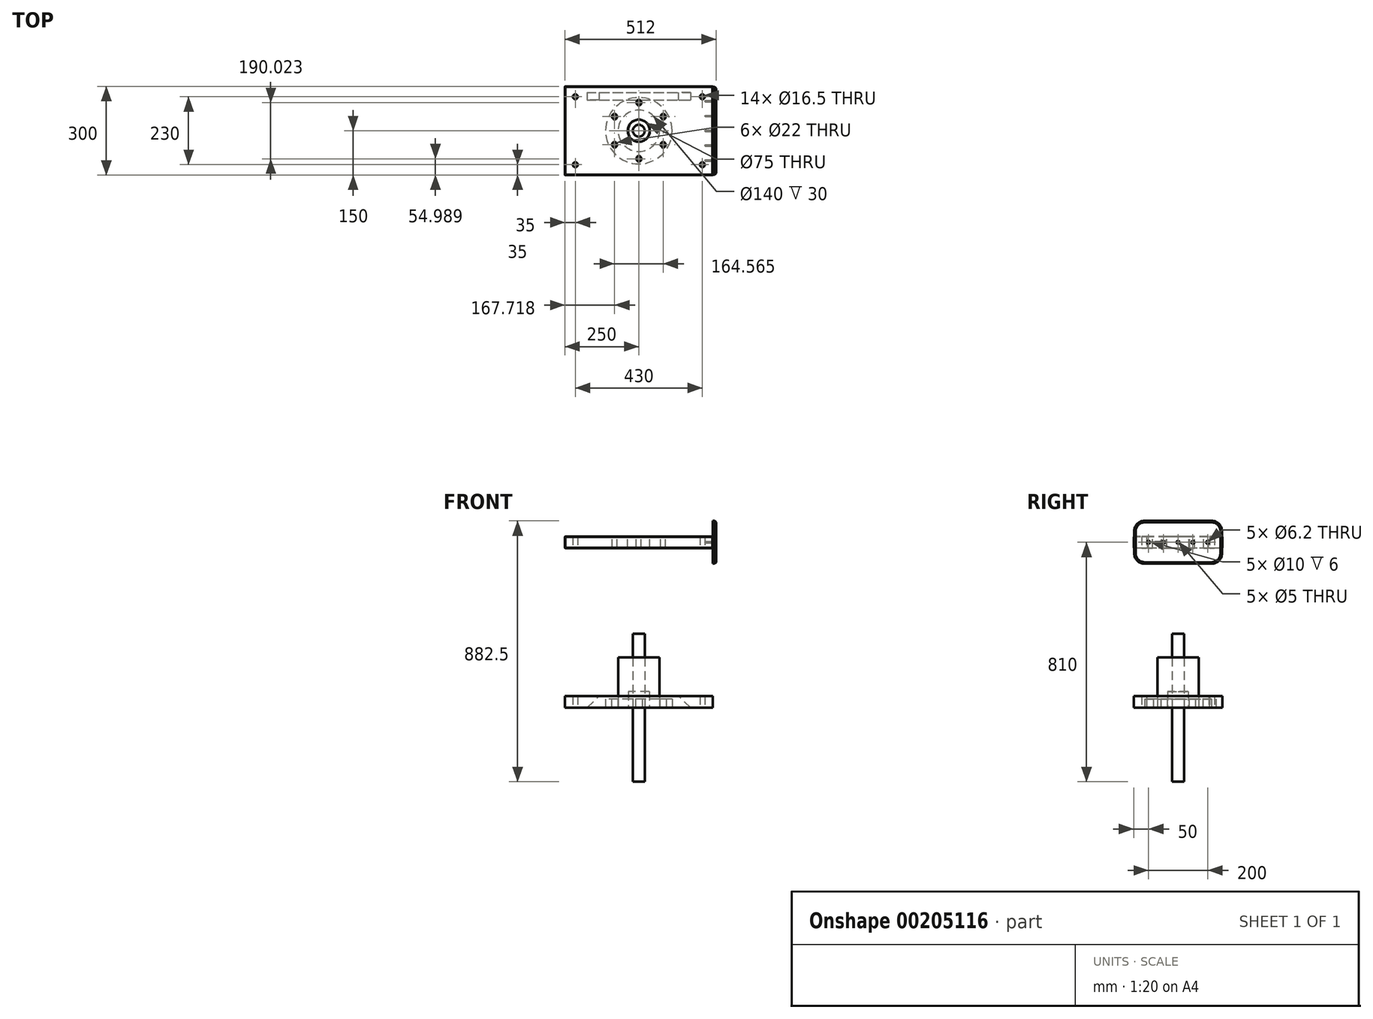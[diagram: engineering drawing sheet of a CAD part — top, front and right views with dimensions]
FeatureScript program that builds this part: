
annotation { "Feature Type Name" : "Feature", "Feature Type Description" : "" }
export const myFeature = defineFeature(function(context is Context, id is Id, definition is map)
    precondition{}
    {
        {
            var Q0;
            Q0=qCreatedBy(makeId("Top.planeOp"),FACE);
            var sketch = newSketch(context, id + "F0", { "sketchPlane" : qUnion([Q0])});
            skLineSegment(sketch, "E0.bottom", {"start": v(250, -150) * mm, "end": v(-250, -150) * mm});
            skLineSegment(sketch, "E0.top", {"start": v(250, 150) * mm, "end": v(-250, 150) * mm});
            skLineSegment(sketch, "E0.left", {"start": v(250, -150) * mm, "end": v(250, 150) * mm});
            skLineSegment(sketch, "E0.right", {"start": v(-250, -150) * mm, "end": v(-250, 150) * mm});
            skPoint(sketch, "E0.middle", {"position": v(0, 0) * mm});
            skCircle(sketch, "E1", {"center": v(-215, 115) * mm, "radius": 8.25 * mm});
            skCircle(sketch, "E2.MirrorC", {"center": v(215, 115) * mm, "radius": 8.25 * mm});
            skCircle(sketch, "E3.MirrorC", {"center": v(-215, -115) * mm, "radius": 8.25 * mm});
            skCircle(sketch, "E4.MirrorC", {"center": v(215, -115) * mm, "radius": 8.25 * mm});
            skSolve(sketch);
        }
        {
            var Q0;
            Q0=makeQuery(id+"F0.imprint","IMPRINT",FACE,{"disambiguationData":[TD([[makeQuery(id+"F0.imprint","IMPRINT",EDGE,{"derivedFrom":sQuery(id+"F0.wireOp",EDGE,"E0.bottom")}),-1.0]])]});
            extrude(context, id + "F1", {"entities" : qUnion([Q0]), "depth" : 40 * mm});
        }
        {
            var Q0;
            Q0=qCreatedBy(makeId("Top.planeOp"),FACE);
            var sketch = newSketch(context, id + "F2", { "sketchPlane" : qUnion([Q0])});
            skLineSegment(sketch, "E5.bottom", {"start": v(-175, 129.44) * mm, "end": v(175, 129.44) * mm});
            skLineSegment(sketch, "E5.top", {"start": v(-175, 104.44) * mm, "end": v(175, 104.44) * mm});
            skLineSegment(sketch, "E5.left", {"start": v(-175, 129.44) * mm, "end": v(-175, 104.44) * mm});
            skLineSegment(sketch, "E5.right", {"start": v(175, 129.44) * mm, "end": v(175, 104.44) * mm});
            skLineSegment(sketch, "E6.MirrorCS", {"start": v(-175, -104.44) * mm, "end": v(175, -104.44) * mm});
            skLineSegment(sketch, "E7.MirrorCS", {"start": v(175, -129.44) * mm, "end": v(175, -104.44) * mm});
            skLineSegment(sketch, "E8.MirrorCS", {"start": v(-175, -129.44) * mm, "end": v(175, -129.44) * mm});
            skLineSegment(sketch, "E9.MirrorCS", {"start": v(-175, -129.44) * mm, "end": v(-175, -104.44) * mm});
            skSolve(sketch);
        }
        {
            var Q0;
            Q0 = qSketchRegion(id + "F2", true);
            extrude(context, id + "F3", {"entities" : qUnion([Q0]), "depth" : 40 * mm});
        }
        {
            var Q0;
            Q0=makeQuery(id+"F3.opExtrude","CAP_EDGE",EDGE,{"disambiguationData":[OSD([sQuery(id+"F2.wireOp",EDGE,"E5.left")])],"isStart":false});
            var Q1;
            Q1=makeQuery(id+"F3.opExtrude","CAP_EDGE",EDGE,{"disambiguationData":[OSD([sQuery(id+"F2.wireOp",EDGE,"E5.right")])],"isStart":false});
            var Q2;
            Q2=makeQuery(id+"F3.opExtrude","CAP_EDGE",EDGE,{"disambiguationData":[OSD([sQuery(id+"F2.wireOp",EDGE,"E7.MirrorCS")])],"isStart":false});
            var Q3;
            Q3=makeQuery(id+"F3.opExtrude","CAP_EDGE",EDGE,{"disambiguationData":[OSD([sQuery(id+"F2.wireOp",EDGE,"E9.MirrorCS")])],"isStart":false});
            chamfer(context, id + "F4", {"entities" : qUnion([Q0, Q1, Q2, Q3]), "width" : 40 * mm, "tangentPropagation" : true});
        }
        {
            var Q0;
            Q0=makeQuery(id+"F3.opExtrude","SWEPT_BODY",BODY,{"disambiguationData":[OSD([sQuery(id+"F2.wireOp",EDGE,"E6.MirrorCS"),sQuery(id+"F2.wireOp",EDGE,"E7.MirrorCS"),sQuery(id+"F2.wireOp",EDGE,"E8.MirrorCS"),sQuery(id+"F2.wireOp",EDGE,"E9.MirrorCS")])]});
            deleteBodies(context, id + "F5", {"entities" : qUnion([Q0])});
        }
        {
            var Q0;
            Q0=qCreatedBy(makeId("Top.planeOp"),FACE);
            var sketch = newSketch(context, id + "F6", { "sketchPlane" : qUnion([Q0])});
            skCircle(sketch, "E10", {"center": v(0, 0) * mm, "radius": 20 * mm});
            skSolve(sketch);
        }
        {
            var Q0;
            Q0 = qSketchRegion(id + "F6", true);
            extrude(context, id + "F7", {"entities" : qUnion([Q0]), "endBound" : BoundingType.SYMMETRIC, "depth" : 500 * mm});
        }
        {
            var Q0;
            Q0=makeQuery(id+"F1.opExtrude","SWEPT_BODY",BODY,{"disambiguationData":[OSD([sQuery(id+"F0.wireOp",EDGE,"E0.bottom"),sQuery(id+"F0.wireOp",EDGE,"E0.top"),sQuery(id+"F0.wireOp",EDGE,"E0.left"),sQuery(id+"F0.wireOp",EDGE,"E0.right"),sQuery(id+"F0.wireOp",EDGE,"E1"),sQuery(id+"F0.wireOp",EDGE,"E2.MirrorC"),sQuery(id+"F0.wireOp",EDGE,"E3.MirrorC"),sQuery(id+"F0.wireOp",EDGE,"E4.MirrorC")])]});
            transform(context, id + "F8", {"entities" : qUnion([Q0]), "transformType" : TransformType.TRANSLATION_3D, "dx" : 0 * mm, "dy" : 0 * mm, "dz" : 540 * mm, "makeCopy" : true});
        }
        {
            var Q0;
            Q0=makeQuery(id+"F8.opPattern","COPY",FACE,{"derivedFrom":makeQuery(id+"F1.opExtrude","CAP_FACE",FACE,{"disambiguationData":[OSD([sQuery(id+"F0.wireOp",EDGE,"E0.bottom"),sQuery(id+"F0.wireOp",EDGE,"E0.top"),sQuery(id+"F0.wireOp",EDGE,"E0.left"),sQuery(id+"F0.wireOp",EDGE,"E0.right"),sQuery(id+"F0.wireOp",EDGE,"E1"),sQuery(id+"F0.wireOp",EDGE,"E2.MirrorC"),sQuery(id+"F0.wireOp",EDGE,"E3.MirrorC"),sQuery(id+"F0.wireOp",EDGE,"E4.MirrorC")])],"isStart":false}),"instanceName":"1"});
            var sketch = newSketch(context, id + "F9", { "sketchPlane" : qUnion([Q0])});
            skCircle(sketch, "E11", {"center": v(0, 0) * mm, "radius": 37.5 * mm});
            skCircle(sketch, "E12", {"center": v(0, 0) * mm, "radius": 70 * mm});
            skCircle(sketch, "E13", {"center": v(0, 0) * mm, "radius": 110 * mm});
            skCircle(sketch, "E14", {"center": v(0, 0) * mm, "radius": 95 * mm});
            skCircle(sketch, "E15", {"center": v(0, 95) * mm, "radius": 11 * mm});
            skCircle(sketch, "E16.1.0", {"center": v(-82.27, 47.5) * mm, "radius": 11 * mm});
            skCircle(sketch, "E16.2.0", {"center": v(-82.27, -47.5) * mm, "radius": 11 * mm});
            skCircle(sketch, "E16.3.0", {"center": v(0, -95) * mm, "radius": 11 * mm});
            skCircle(sketch, "E16.4.0", {"center": v(82.27, -47.5) * mm, "radius": 11 * mm});
            skCircle(sketch, "E16.5.0", {"center": v(82.27, 47.5) * mm, "radius": 11 * mm});
            skCircle(sketch, "E17", {"center": v(0, 95) * mm, "radius": 8.25 * mm});
            skCircle(sketch, "E18.1.0", {"center": v(-82.27, 47.5) * mm, "radius": 8.25 * mm});
            skCircle(sketch, "E18.2.0", {"center": v(-82.27, -47.5) * mm, "radius": 8.25 * mm});
            skCircle(sketch, "E19.1.3.0", {"center": v(0, -95) * mm, "radius": 8.25 * mm});
            skCircle(sketch, "E19.1.4.0", {"center": v(82.27, -47.5) * mm, "radius": 8.25 * mm});
            skCircle(sketch, "E19.1.5.0", {"center": v(82.27, 47.5) * mm, "radius": 8.25 * mm});
            skSolve(sketch);
        }
        {
            var Q0;
            Q0=sQuery(id+"F9.wireOp",VERTEX,"E11.center");
            var Q1;
            Q1=makeQuery(id+"F8.opPattern","COPY",BODY,{"derivedFrom":makeQuery(id+"F1.opExtrude","SWEPT_BODY",BODY,{"disambiguationData":[OSD([sQuery(id+"F0.wireOp",EDGE,"E0.bottom"),sQuery(id+"F0.wireOp",EDGE,"E0.top"),sQuery(id+"F0.wireOp",EDGE,"E0.left"),sQuery(id+"F0.wireOp",EDGE,"E0.right"),sQuery(id+"F0.wireOp",EDGE,"E1"),sQuery(id+"F0.wireOp",EDGE,"E2.MirrorC"),sQuery(id+"F0.wireOp",EDGE,"E3.MirrorC"),sQuery(id+"F0.wireOp",EDGE,"E4.MirrorC")])]}),"instanceName":"1"});
            hole(context, id + "F10", {"style" : HoleStyle.SIMPLE, "endStyle" : HoleEndStyle.THROUGH, "holeDiameter" : 75 * mm, "locations" : qUnion([Q0]), "scope" : qUnion([Q1]), "isTappedThrough" : true});
        }
        {
            var Q0;
            Q0=sQuery(id+"F9.wireOp",VERTEX,"E18.1.0.center");
            var Q1;
            Q1=sQuery(id+"F9.wireOp",VERTEX,"E17.center");
            var Q2;
            Q2=sQuery(id+"F9.wireOp",VERTEX,"E19.1.5.0.center");
            var Q3;
            Q3=sQuery(id+"F9.wireOp",VERTEX,"E19.1.4.0.center");
            var Q4;
            Q4=sQuery(id+"F9.wireOp",VERTEX,"E19.1.3.0.center");
            var Q5;
            Q5=sQuery(id+"F9.wireOp",VERTEX,"E18.2.0.center");
            var Q6;
            Q6=makeQuery(id+"F8.opPattern","COPY",BODY,{"derivedFrom":makeQuery(id+"F1.opExtrude","SWEPT_BODY",BODY,{"disambiguationData":[OSD([sQuery(id+"F0.wireOp",EDGE,"E0.bottom"),sQuery(id+"F0.wireOp",EDGE,"E0.top"),sQuery(id+"F0.wireOp",EDGE,"E0.left"),sQuery(id+"F0.wireOp",EDGE,"E0.right"),sQuery(id+"F0.wireOp",EDGE,"E1"),sQuery(id+"F0.wireOp",EDGE,"E2.MirrorC"),sQuery(id+"F0.wireOp",EDGE,"E3.MirrorC"),sQuery(id+"F0.wireOp",EDGE,"E4.MirrorC")])]}),"instanceName":"1"});
            hole(context, id + "F11", {"style" : HoleStyle.SIMPLE, "endStyle" : HoleEndStyle.THROUGH, "holeDiameter" : 16.5 * mm, "locations" : qUnion([Q0, Q1, Q2, Q3, Q4, Q5]), "scope" : qUnion([Q6]), "isTappedThrough" : true});
        }
        {
            var Q0;
            Q0=makeQuery(id+"F8.opPattern","COPY",EDGE,{"derivedFrom":makeQuery(id+"F1.opExtrude","CAP_EDGE",EDGE,{"disambiguationData":[OSD([sQuery(id+"F0.wireOp",EDGE,"E0.top")])],"isStart":false}),"instanceName":"1"});
            var Q1;
            Q1=makeQuery(id+"F8.opPattern","COPY",EDGE,{"derivedFrom":makeQuery(id+"F1.opExtrude","CAP_EDGE",EDGE,{"disambiguationData":[OSD([sQuery(id+"F0.wireOp",EDGE,"E0.right")])],"isStart":false}),"instanceName":"1"});
            var Q2;
            Q2=makeQuery(id+"F8.opPattern","COPY",EDGE,{"derivedFrom":makeQuery(id+"F1.opExtrude","SWEPT_EDGE",EDGE,{"disambiguationData":[OSD([sQuery(id+"F0.wireOp",EDGE,"E0.top"),sQuery(id+"F0.wireOp",EDGE,"E0.right")])]}),"instanceName":"1"});
            var Q3;
            Q3=makeQuery(id+"F8.opPattern","COPY",EDGE,{"derivedFrom":makeQuery(id+"F1.opExtrude","CAP_EDGE",EDGE,{"disambiguationData":[OSD([sQuery(id+"F0.wireOp",EDGE,"E0.right")])],"isStart":true}),"instanceName":"1"});
            var Q4;
            Q4=makeQuery(id+"F8.opPattern","COPY",EDGE,{"derivedFrom":makeQuery(id+"F1.opExtrude","SWEPT_EDGE",EDGE,{"disambiguationData":[OSD([sQuery(id+"F0.wireOp",EDGE,"E0.bottom"),sQuery(id+"F0.wireOp",EDGE,"E0.right")])]}),"instanceName":"1"});
            var Q5;
            Q5=makeQuery(id+"F8.opPattern","COPY",EDGE,{"derivedFrom":makeQuery(id+"F1.opExtrude","CAP_EDGE",EDGE,{"disambiguationData":[OSD([sQuery(id+"F0.wireOp",EDGE,"E0.bottom")])],"isStart":false}),"instanceName":"1"});
            var Q6;
            Q6=makeQuery(id+"F8.opPattern","COPY",EDGE,{"derivedFrom":makeQuery(id+"F1.opExtrude","CAP_EDGE",EDGE,{"disambiguationData":[OSD([sQuery(id+"F0.wireOp",EDGE,"E0.bottom")])],"isStart":true}),"instanceName":"1"});
            var Q7;
            Q7=makeQuery(id+"F8.opPattern","COPY",EDGE,{"derivedFrom":makeQuery(id+"F1.opExtrude","CAP_EDGE",EDGE,{"disambiguationData":[OSD([sQuery(id+"F0.wireOp",EDGE,"E0.left")])],"isStart":false}),"instanceName":"1"});
            var Q8;
            Q8=makeQuery(id+"F8.opPattern","COPY",EDGE,{"derivedFrom":makeQuery(id+"F1.opExtrude","SWEPT_EDGE",EDGE,{"disambiguationData":[OSD([sQuery(id+"F0.wireOp",EDGE,"E0.bottom"),sQuery(id+"F0.wireOp",EDGE,"E0.left")])]}),"instanceName":"1"});
            var Q9;
            Q9=makeQuery(id+"F8.opPattern","COPY",EDGE,{"derivedFrom":makeQuery(id+"F1.opExtrude","CAP_EDGE",EDGE,{"disambiguationData":[OSD([sQuery(id+"F0.wireOp",EDGE,"E0.left")])],"isStart":true}),"instanceName":"1"});
            var Q10;
            Q10=makeQuery(id+"F8.opPattern","COPY",EDGE,{"derivedFrom":makeQuery(id+"F1.opExtrude","CAP_EDGE",EDGE,{"disambiguationData":[OSD([sQuery(id+"F0.wireOp",EDGE,"E0.top")])],"isStart":true}),"instanceName":"1"});
            var Q11;
            Q11=makeQuery(id+"F8.opPattern","COPY",EDGE,{"derivedFrom":makeQuery(id+"F1.opExtrude","SWEPT_EDGE",EDGE,{"disambiguationData":[OSD([sQuery(id+"F0.wireOp",EDGE,"E0.top"),sQuery(id+"F0.wireOp",EDGE,"E0.left")])]}),"instanceName":"1"});
            var Q12;
            Q12=makeQuery(id+"F10.hole-0.boolean.opBoolean","COPY",EDGE,{"derivedFrom":makeQuery(id+"F10.hole-0.opRevolve","SWEPT_EDGE",EDGE,{"disambiguationData":[OSD([sQuery(id+"F10.hole-0.sketch.wireOp",EDGE,"core_line_2"),sQuery(id+"F10.hole-0.sketch.wireOp",EDGE,"core_line_3")])]})});
            var Q13;
            Q13=makeQuery(id+"F10.hole-0.boolean.opBoolean","INTERSECT",EDGE,{"derivedFrom":[makeQuery(id+"F8.opPattern","COPY",FACE,{"derivedFrom":makeQuery(id+"F1.opExtrude","CAP_FACE",FACE,{"disambiguationData":[OSD([sQuery(id+"F0.wireOp",EDGE,"E0.bottom"),sQuery(id+"F0.wireOp",EDGE,"E0.top"),sQuery(id+"F0.wireOp",EDGE,"E0.left"),sQuery(id+"F0.wireOp",EDGE,"E0.right"),sQuery(id+"F0.wireOp",EDGE,"E1"),sQuery(id+"F0.wireOp",EDGE,"E2.MirrorC"),sQuery(id+"F0.wireOp",EDGE,"E3.MirrorC"),sQuery(id+"F0.wireOp",EDGE,"E4.MirrorC")])],"isStart":true}),"instanceName":"1"}),makeQuery(id+"F10.hole-0.opRevolve","SWEPT_FACE",FACE,{"disambiguationData":[OSD([sQuery(id+"F10.hole-0.sketch.wireOp",EDGE,"core_line_2")])]})]});
            chamfer(context, id + "F12", {"entities" : qUnion([Q0, Q1, Q2, Q3, Q4, Q5, Q6, Q7, Q8, Q9, Q10, Q11, Q12, Q13]), "width" : 1.5 * mm, "tangentPropagation" : true});
        }
        {
            var Q0;
            Q0=qCreatedBy(makeId("Top.planeOp"),FACE);
            var sketch = newSketch(context, id + "F13", { "sketchPlane" : qUnion([Q0])});
            skCircle(sketch, "E20", {"center": v(0, 0) * mm, "radius": 70 * mm});
            skCircle(sketch, "E21", {"center": v(0, 95.01) * mm, "radius": 11 * mm});
            skCircle(sketch, "E22", {"center": v(0, 0) * mm, "radius": 112.5 * mm});
            skCircle(sketch, "E23.1.0", {"center": v(-82.28, 47.5) * mm, "radius": 11 * mm});
            skCircle(sketch, "E23.2.0", {"center": v(-82.28, -47.5) * mm, "radius": 11 * mm});
            skCircle(sketch, "E23.3.0", {"center": v(0, -95.01) * mm, "radius": 11 * mm});
            skCircle(sketch, "E23.4.0", {"center": v(82.28, -47.5) * mm, "radius": 11 * mm});
            skCircle(sketch, "E23.5.0", {"center": v(82.28, 47.5) * mm, "radius": 11 * mm});
            skSolve(sketch);
        }
        {
            var Q0;
            Q0 = qSketchRegion(id + "F13", true);
            extrude(context, id + "F14", {"entities" : qUnion([Q0]), "depth" : 30 * mm});
        }
        {
            var Q0;
            Q0=qCreatedBy(makeId("Top.planeOp"),FACE);
            var sketch = newSketch(context, id + "F15", { "sketchPlane" : qUnion([Q0])});
            skCircle(sketch, "E24", {"center": v(0, 0) * mm, "radius": 70 * mm});
            skSolve(sketch);
        }
        {
            var Q0;
            Q0 = qSketchRegion(id + "F15", true);
            extrude(context, id + "F16", {"entities" : qUnion([Q0]), "depth" : 170 * mm});
        }
        {
            var Q0;
            Q0=qCreatedBy(makeId("Top.planeOp"),FACE);
            var sketch = newSketch(context, id + "F17", { "sketchPlane" : qUnion([Q0])});
            skCircle(sketch, "E25", {"center": v(0, 0) * mm, "radius": 35 * mm});
            skSolve(sketch);
        }
        {
            var Q0;
            Q0 = qSketchRegion(id + "F17", true);
            extrude(context, id + "F18", {"entities" : qUnion([Q0]), "depth" : 55 * mm});
        }
        {
            var Q0;
            Q0=makeQuery(id+"F8.opPattern","COPY",FACE,{"derivedFrom":makeQuery(id+"F1.opExtrude","SWEPT_FACE",FACE,{"disambiguationData":[OSD([sQuery(id+"F0.wireOp",EDGE,"E0.left")])]}),"instanceName":"1"});
            var sketch = newSketch(context, id + "F19", { "sketchPlane" : qUnion([Q0])});
            skLineSegment(sketch, "E26", {"start": v(-148.5, 560) * mm, "end": v(148.5, 560) * mm});
            skPoint(sketch, "E27", {"position": v(0, 560) * mm});
            skPoint(sketch, "E28.1.0.0", {"position": v(50, 560) * mm});
            skPoint(sketch, "E28.2.0.0", {"position": v(100, 560) * mm});
            skLineSegment(sketch, "E28.direction1", {"start": v(0, 560) * mm, "end": v(50, 560) * mm, "construction": true});
            skPoint(sketch, "E29.1.0.0", {"position": v(-50, 560) * mm});
            skPoint(sketch, "E29.2.0.0", {"position": v(-100, 560) * mm});
            skLineSegment(sketch, "E29.direction1", {"start": v(0, 560) * mm, "end": v(-50, 560) * mm, "construction": true});
            skLineSegment(sketch, "E30.bottom", {"start": v(-113.5, 632.5) * mm, "end": v(113.5, 632.5) * mm});
            skLineSegment(sketch, "E30.top", {"start": v(-113.5, 487.5) * mm, "end": v(113.5, 487.5) * mm});
            skLineSegment(sketch, "E30.left", {"start": v(-148.5, 597.5) * mm, "end": v(-148.5, 522.5) * mm});
            skLineSegment(sketch, "E30.right", {"start": v(148.5, 597.5) * mm, "end": v(148.5, 522.5) * mm});
            skPoint(sketch, "E31.visualSharp", {"position": v(-148.5, 632.5) * mm});
            skArc(sketch, "E31.filletArc", {"start": v(-113.5, 632.5) * mm, "mid": v(-138.25, 622.25) * mm, "end": v(-148.5, 597.5) * mm});
            skPoint(sketch, "E32.visualSharp", {"position": v(148.5, 632.5) * mm});
            skArc(sketch, "E32.filletArc", {"start": v(148.5, 597.5) * mm, "mid": v(138.25, 622.25) * mm, "end": v(113.5, 632.5) * mm});
            skPoint(sketch, "E33.visualSharp", {"position": v(148.5, 487.5) * mm});
            skArc(sketch, "E33.filletArc", {"start": v(113.5, 487.5) * mm, "mid": v(138.25, 497.75) * mm, "end": v(148.5, 522.5) * mm});
            skPoint(sketch, "E34.visualSharp", {"position": v(-148.5, 487.5) * mm});
            skArc(sketch, "E34.filletArc", {"start": v(-148.5, 522.5) * mm, "mid": v(-138.25, 497.75) * mm, "end": v(-113.5, 487.5) * mm});
            skSolve(sketch);
        }
        {
            var Q0;
            Q0=makeQuery(id+"F19.imprint","IMPRINT",FACE,{"disambiguationData":[TD([[makeQuery(id+"F19.imprint","IMPRINT",EDGE,{"derivedFrom":sQuery(id+"F19.wireOp",EDGE,"E30.top")}),1.0]])]});
            var Q1;
            {var subQ0=sQuery(id+"F19.wireOp",EDGE,"E26");Q1=makeQuery(id+"F19.imprint","IMPRINT",FACE,{"disambiguationData":[TD([[makeQuery(id+"F19.imprint","IMPRINT",EDGE,{"derivedFrom":subQ0}),-1.0]])]});}
            var Q2;
            {var subQ0=sQuery(id+"F19.wireOp",EDGE,"E26");Q2=makeQuery(id+"F19.imprint","IMPRINT",FACE,{"disambiguationData":[TD([[makeQuery(id+"F19.imprint","IMPRINT",EDGE,{"derivedFrom":subQ0}),1.0]])]});}
            var Q3;
            Q3=makeQuery(id+"F19.imprint","IMPRINT",FACE,{"disambiguationData":[TD([[makeQuery(id+"F19.imprint","IMPRINT",EDGE,{"derivedFrom":sQuery(id+"F19.wireOp",EDGE,"E30.bottom")}),-1.0]])]});
            extrude(context, id + "F20", {"entities" : qUnion([Q0, Q1, Q2, Q3]), "depth" : 12 * mm, "offsetDistance" : 25 * mm});
        }
        {
            var Q0;
            Q0=makeQuery(id+"F20.opExtrude","CAP_FACE",FACE,{"disambiguationData":[OSD([sQuery(id+"F19.wireOp",EDGE,"E30.bottom"),sQuery(id+"F19.wireOp",EDGE,"E30.top"),sQuery(id+"F19.wireOp",EDGE,"E30.left"),sQuery(id+"F19.wireOp",EDGE,"E30.right"),sQuery(id+"F19.wireOp",EDGE,"E31.filletArc"),sQuery(id+"F19.wireOp",EDGE,"E32.filletArc"),sQuery(id+"F19.wireOp",EDGE,"E33.filletArc"),sQuery(id+"F19.wireOp",EDGE,"E34.filletArc")])],"isStart":false});
            var sketch = newSketch(context, id + "F21", { "sketchPlane" : qUnion([Q0])});
            skPoint(sketch, "E35", {"position": v(0, 560) * mm});
            skPoint(sketch, "E35.positionSnap0", {"position": v(0, 487.5) * mm});
            skPoint(sketch, "E35.positionSnap1", {"position": v(148.5, 560) * mm});
            skPoint(sketch, "E36", {"position": v(-50, 560) * mm});
            skPoint(sketch, "E37", {"position": v(-100, 560) * mm});
            skPoint(sketch, "E38", {"position": v(50, 560) * mm});
            skPoint(sketch, "E39", {"position": v(100, 560) * mm});
            skSolve(sketch);
        }
        {
            var Q0;
            Q0=sQuery(id+"F21.wireOp",VERTEX,"E37");
            var Q1;
            Q1=sQuery(id+"F21.wireOp",VERTEX,"E36");
            var Q2;
            Q2=sQuery(id+"F21.wireOp",VERTEX,"E35");
            var Q3;
            Q3=sQuery(id+"F21.wireOp",VERTEX,"E38");
            var Q4;
            Q4=sQuery(id+"F21.wireOp",VERTEX,"E39");
            var Q5;
            Q5=makeQuery(id+"F8.opPattern","COPY",BODY,{"derivedFrom":makeQuery(id+"F1.opExtrude","SWEPT_BODY",BODY,{"disambiguationData":[OSD([sQuery(id+"F0.wireOp",EDGE,"E0.bottom"),sQuery(id+"F0.wireOp",EDGE,"E0.top"),sQuery(id+"F0.wireOp",EDGE,"E0.left"),sQuery(id+"F0.wireOp",EDGE,"E0.right"),sQuery(id+"F0.wireOp",EDGE,"E1"),sQuery(id+"F0.wireOp",EDGE,"E2.MirrorC"),sQuery(id+"F0.wireOp",EDGE,"E3.MirrorC"),sQuery(id+"F0.wireOp",EDGE,"E4.MirrorC")])]}),"instanceName":"1"});
            var Q6;
            Q6=makeQuery(id+"F20.opExtrude","SWEPT_BODY",BODY,{"disambiguationData":[OSD([sQuery(id+"F19.wireOp",EDGE,"E30.bottom"),sQuery(id+"F19.wireOp",EDGE,"E30.top"),sQuery(id+"F19.wireOp",EDGE,"E30.left"),sQuery(id+"F19.wireOp",EDGE,"E30.right"),sQuery(id+"F19.wireOp",EDGE,"E31.filletArc"),sQuery(id+"F19.wireOp",EDGE,"E32.filletArc"),sQuery(id+"F19.wireOp",EDGE,"E33.filletArc"),sQuery(id+"F19.wireOp",EDGE,"E34.filletArc")])]});
            hole(context, id + "F22", {"style" : HoleStyle.C_BORE, "endStyle" : HoleEndStyle.BLIND_IN_LAST, "holeDiameter" : 6.2 * mm, "cBoreDiameter" : 10 * mm, "cBoreDepth" : 6 * mm, "tapDrillDiameter" : 5 * mm, "majorDiameter" : 5 * mm, "holeDepth" : 25 * mm, "isTappedThrough" : true, "tappedDepth" : 12 * mm, "tapClearance" : 3, "startFromSketch" : true, "locations" : qUnion([Q0, Q1, Q2, Q3, Q4]), "scope" : qUnion([Q5, Q6])});
        }
        {
            var Q0;
            Q0=makeQuery(id+"F20.opExtrude","CAP_EDGE",EDGE,{"disambiguationData":[OSD([sQuery(id+"F19.wireOp",EDGE,"E30.left")])],"isStart":false});
            chamfer(context, id + "F23", {"entities" : qUnion([Q0]), "width" : 5 * mm, "tangentPropagation" : true});
        }
    });
